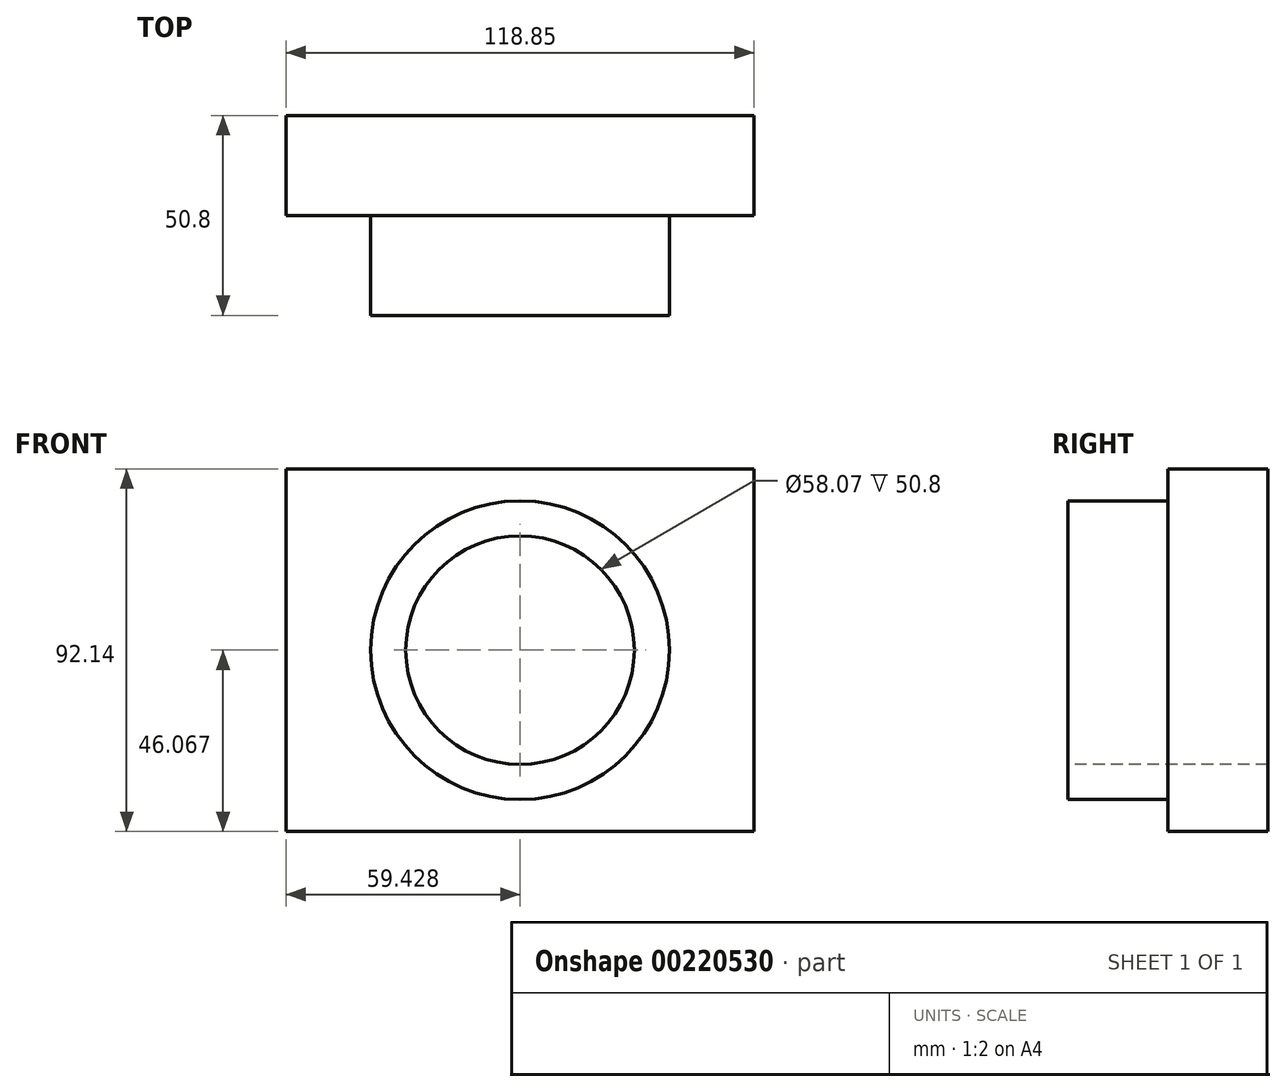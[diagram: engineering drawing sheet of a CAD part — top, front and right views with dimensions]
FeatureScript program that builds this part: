
annotation { "Feature Type Name" : "Feature", "Feature Type Description" : "" }
export const myFeature = defineFeature(function(context is Context, id is Id, definition is map)
    precondition{}
    {
        {
            var Q0;
            Q0=qCreatedBy(makeId("Front.planeOp"),FACE);
            var sketch = newSketch(context, id + "F0", { "sketchPlane" : qUnion([Q0])});
            skLineSegment(sketch, "E0.bottom", {"start": v(-54.65, 41.54) * mm, "end": v(64.2, 41.54) * mm});
            skLineSegment(sketch, "E0.top", {"start": v(-54.65, -50.6) * mm, "end": v(64.2, -50.6) * mm});
            skLineSegment(sketch, "E0.left", {"start": v(-54.65, 41.54) * mm, "end": v(-54.65, -50.6) * mm});
            skLineSegment(sketch, "E0.right", {"start": v(64.2, 41.54) * mm, "end": v(64.2, -50.6) * mm});
            skSolve(sketch);
        }
        {
            var Q0;
            Q0=makeQuery(id+"F0.imprint","IMPRINT",FACE,{"disambiguationData":[TD([[makeQuery(id+"F0.imprint","IMPRINT",EDGE,{"derivedFrom":sQuery(id+"F0.wireOp",EDGE,"E0.bottom")}),-1.0]])]});
            extrude(context, id + "F1", {"entities" : qUnion([Q0]), "depth" : 25.4 * mm});
        }
        {
            var Q0;
            Q0=makeQuery(id+"F1.opExtrude","CAP_FACE",FACE,{"disambiguationData":[OSD([sQuery(id+"F0.wireOp",EDGE,"E0.bottom"),sQuery(id+"F0.wireOp",EDGE,"E0.top"),sQuery(id+"F0.wireOp",EDGE,"E0.left"),sQuery(id+"F0.wireOp",EDGE,"E0.right")])],"isStart":false});
            var sketch = newSketch(context, id + "F2", { "sketchPlane" : qUnion([Q0])});
            skCircle(sketch, "E1", {"center": v(4.78, -4.53) * mm, "radius": 37.93 * mm});
            skPoint(sketch, "E1.centerSnap0", {"position": v(-54.65, -4.53) * mm});
            skPoint(sketch, "E1.centerSnap1", {"position": v(4.78, 41.54) * mm});
            skSolve(sketch);
        }
        {
            var Q0;
            Q0=makeQuery(id+"F2.imprint","IMPRINT",FACE,{"disambiguationData":[TD([[makeQuery(id+"F2.imprint","IMPRINT",EDGE,{"derivedFrom":sQuery(id+"F2.wireOp",EDGE,"E1")}),1.0]])]});
            extrude(context, id + "F3", {"entities" : qUnion([Q0]), "operationType" : NewBodyOperationType.ADD, "depth" : 25.4 * mm});
        }
        {
            var Q0;
            Q0=makeQuery(id+"F3.opExtrude","CAP_FACE",FACE,{"disambiguationData":[OSD([sQuery(id+"F2.wireOp",EDGE,"E1")])],"isStart":false});
            var sketch = newSketch(context, id + "F4", { "sketchPlane" : qUnion([Q0])});
            skCircle(sketch, "E2", {"center": v(4.78, -4.53) * mm, "radius": 29.03 * mm});
            skSolve(sketch);
        }
        {
            var Q0;
            Q0=makeQuery(id+"F4.imprint","IMPRINT",FACE,{"disambiguationData":[TD([[makeQuery(id+"F4.imprint","IMPRINT",EDGE,{"derivedFrom":sQuery(id+"F4.wireOp",EDGE,"E2")}),1.0]])]});
            extrude(context, id + "F5", {"entities" : qUnion([Q0]), "operationType" : NewBodyOperationType.REMOVE, "oppositeDirection" : true, "depth" : 76.2 * mm});
        }
    });
